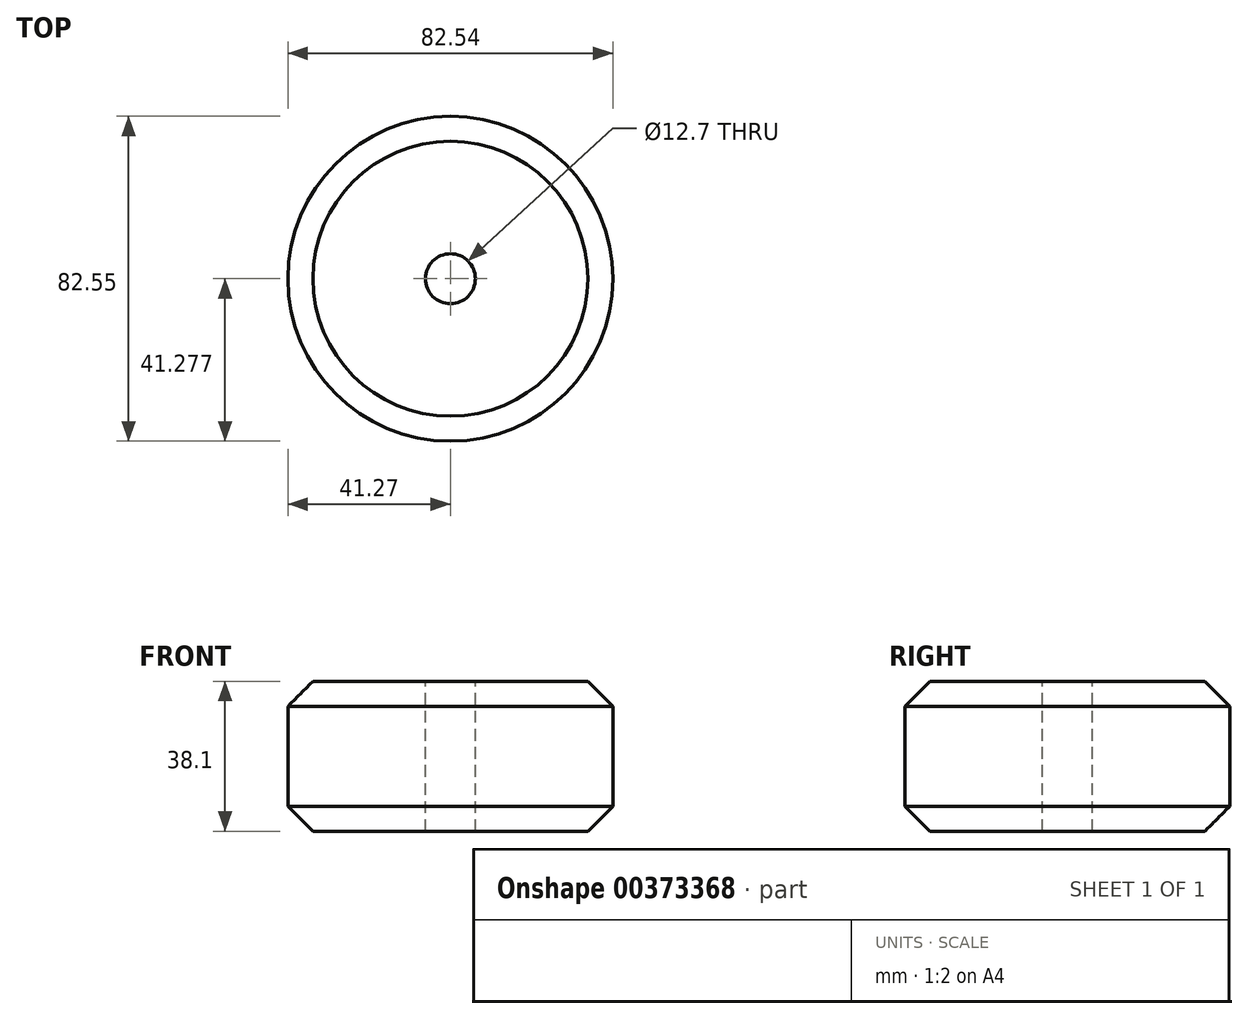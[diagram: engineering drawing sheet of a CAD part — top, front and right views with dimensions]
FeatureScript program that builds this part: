
annotation { "Feature Type Name" : "Feature", "Feature Type Description" : "" }
export const myFeature = defineFeature(function(context is Context, id is Id, definition is map)
    precondition{}
    {
        {
            var Q0;
            Q0=qCreatedBy(makeId("Right.planeOp"),FACE);
            var sketch = newSketch(context, id + "F0", { "sketchPlane" : qUnion([Q0])});
            skLineSegment(sketch, "E0.bottom", {"start": v(-46.74, 43.27) * mm, "end": v(-11.81, 43.27) * mm});
            skLineSegment(sketch, "E0.top", {"start": v(-46.74, 5.17) * mm, "end": v(-11.81, 5.17) * mm});
            skLineSegment(sketch, "E0.left", {"start": v(-46.74, 43.27) * mm, "end": v(-46.74, 5.17) * mm});
            skLineSegment(sketch, "E0.right", {"start": v(-11.81, 43.27) * mm, "end": v(-11.81, 5.17) * mm});
            skLineSegment(sketch, "E1", {"start": v(-5.46, 57.02) * mm, "end": v(-5.46, -9.5) * mm});
            skSolve(sketch);
        }
        {
            var Q0;
            Q0 = qSketchRegion(id + "F0", true);
            var Q1;
            Q1=sQuery(id+"F0.wireOp",EDGE,"E1");
            revolve(context, id + "F1", {"entities" : qUnion([Q0]), "axis" : qUnion([Q1]), "revolveType" : RevolveType.FULL});
        }
        {
            var Q0;
            Q0=makeQuery(id+"F1.opRevolve","SWEPT_EDGE",EDGE,{"disambiguationData":[OSD([sQuery(id+"F0.wireOp",EDGE,"E0.bottom"),sQuery(id+"F0.wireOp",EDGE,"E0.left")])]});
            var Q1;
            Q1=makeQuery(id+"F1.opRevolve","SWEPT_EDGE",EDGE,{"disambiguationData":[OSD([sQuery(id+"F0.wireOp",EDGE,"E0.top"),sQuery(id+"F0.wireOp",EDGE,"E0.left")])]});
            chamfer(context, id + "F2", {"entities" : qUnion([Q0, Q1]), "width" : 6.35 * mm, "tangentPropagation" : true});
        }
    });
